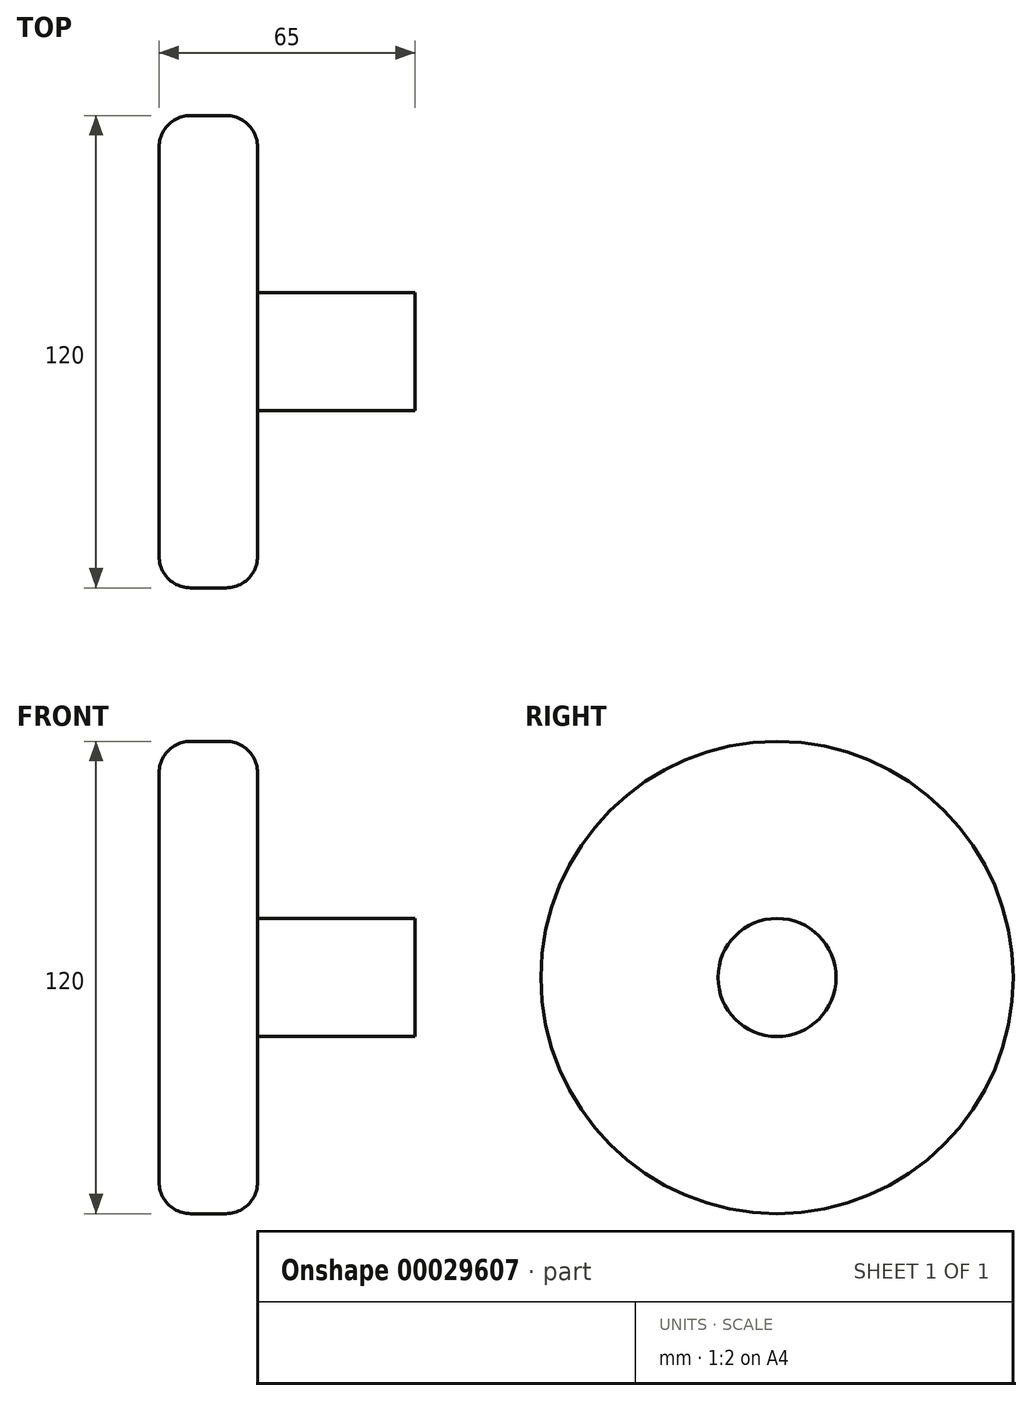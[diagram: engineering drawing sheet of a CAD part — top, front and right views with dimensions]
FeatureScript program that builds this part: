
annotation { "Feature Type Name" : "Feature", "Feature Type Description" : "" }
export const myFeature = defineFeature(function(context is Context, id is Id, definition is map)
    precondition{}
    {
        {
            var Q0;
            Q0=qCreatedBy(makeId("Right.planeOp"),FACE);
            var sketch = newSketch(context, id + "F0", { "sketchPlane" : qUnion([Q0])});
            skCircle(sketch, "E0", {"center": v(0, 0) * mm, "radius": 60 * mm});
            skCircle(sketch, "E1", {"center": v(0, 0) * mm, "radius": 15 * mm});
            skSolve(sketch);
        }
        {
            var Q0;
            Q0=makeQuery(id+"F0.imprint","IMPRINT",FACE,{"disambiguationData":[TD([[makeQuery(id+"F0.imprint","IMPRINT",EDGE,{"derivedFrom":sQuery(id+"F0.wireOp",EDGE,"E0")}),1.0]])]});
            var Q1;
            Q1=makeQuery(id+"F0.imprint","IMPRINT",FACE,{"disambiguationData":[TD([[makeQuery(id+"F0.imprint","IMPRINT",EDGE,{"derivedFrom":sQuery(id+"F0.wireOp",EDGE,"E1")}),1.0]])]});
            extrude(context, id + "F1", {"entities" : qUnion([Q0, Q1]), "oppositeDirection" : true, "depth" : 25 * mm});
        }
        {
            var Q0;
            Q0=makeQuery(id+"F0.imprint","IMPRINT",FACE,{"disambiguationData":[TD([[makeQuery(id+"F0.imprint","IMPRINT",EDGE,{"derivedFrom":sQuery(id+"F0.wireOp",EDGE,"E1")}),1.0]])]});
            extrude(context, id + "F2", {"entities" : qUnion([Q0]), "operationType" : NewBodyOperationType.ADD, "depth" : 40 * mm});
        }
        {
            var Q0;
            Q0=makeQuery(id+"F1.opExtrude","CAP_EDGE",EDGE,{"disambiguationData":[OSD([sQuery(id+"F0.wireOp",EDGE,"E0")])],"isStart":true});
            var Q1;
            Q1=makeQuery(id+"F1.opExtrude","CAP_EDGE",EDGE,{"disambiguationData":[OSD([sQuery(id+"F0.wireOp",EDGE,"E0")])],"isStart":false});
            fillet(context, id + "F3", {"entities" : qUnion([Q0, Q1]), "radius" : 8 * mm, "tangentPropagation" : true, "allowEdgeOverflow" : false});
        }
    });
